# Revit family: BIM_Ленточный_двухскатный_зенитный_фонарь_M8CITY_Д_ВЕНТ-ДЫМ_со_створками_30_град
name_source: partatom
category: Окна
units: mm (PartAtom-declared; Revit-internal decimal feet)

## family parameters
Всегда вертикально = Нет
Общий = Нет
Основа = Крыша
При загрузке вырезать с полостями = Нет
Точка расчета площади = Нет

## types (1)
- Зенитный фонарь M8CITY
    230В двойной = Нет
    N арок = 7
    N растров = 8
    URL = www.m8city.by
    Бренд = M8CITY
    Вид створки = 1
    Видимость привода двойного = Нет
    Видимость створки = Да
    Видимость створки двойной = Нет
    Высота = 673 мм
    Высота основания = 600 мм
    Длина = 8000 мм
    Длина проема = 8000 мм
    Длина проема ввод = 8000 мм
    Длина створки = 1900 мм
    Длина створки ном = 1732.1 мм
    Изготовитель = ООО М8 Сити Про
    Количество приводов = 3
    Количество створок = 3
    Количество створок ном = 3
    Количество типовых растров = 7
    Крайний растр = 864.5 мм
    Материал заполнения = <По категории>
    Описание = Ленточный зенитный фонарь M8CITY в премиальном исполнении ВЕНТ/ДЫМ двухскатный
    Отметка по умолчанию = 0 мм
    Привод = 2
    Привод двойной створки = 0
    Смещение массива = 1924.5 мм
    Смещение массива приводов = 1924.5 мм
    Телефон = +375 17 311 09 02, +7 495 946 99 02, +380 50 120 51 80
    Угол = 0.866025
    Шаг массива = 2120 мм
    Шаг массива приводов = 2120 мм
    Шаг типовой = 1060 мм
    Ширина = 3000 мм
    Ширина проема = 3000 мм
    Ширина проема ввод = 3000 мм
